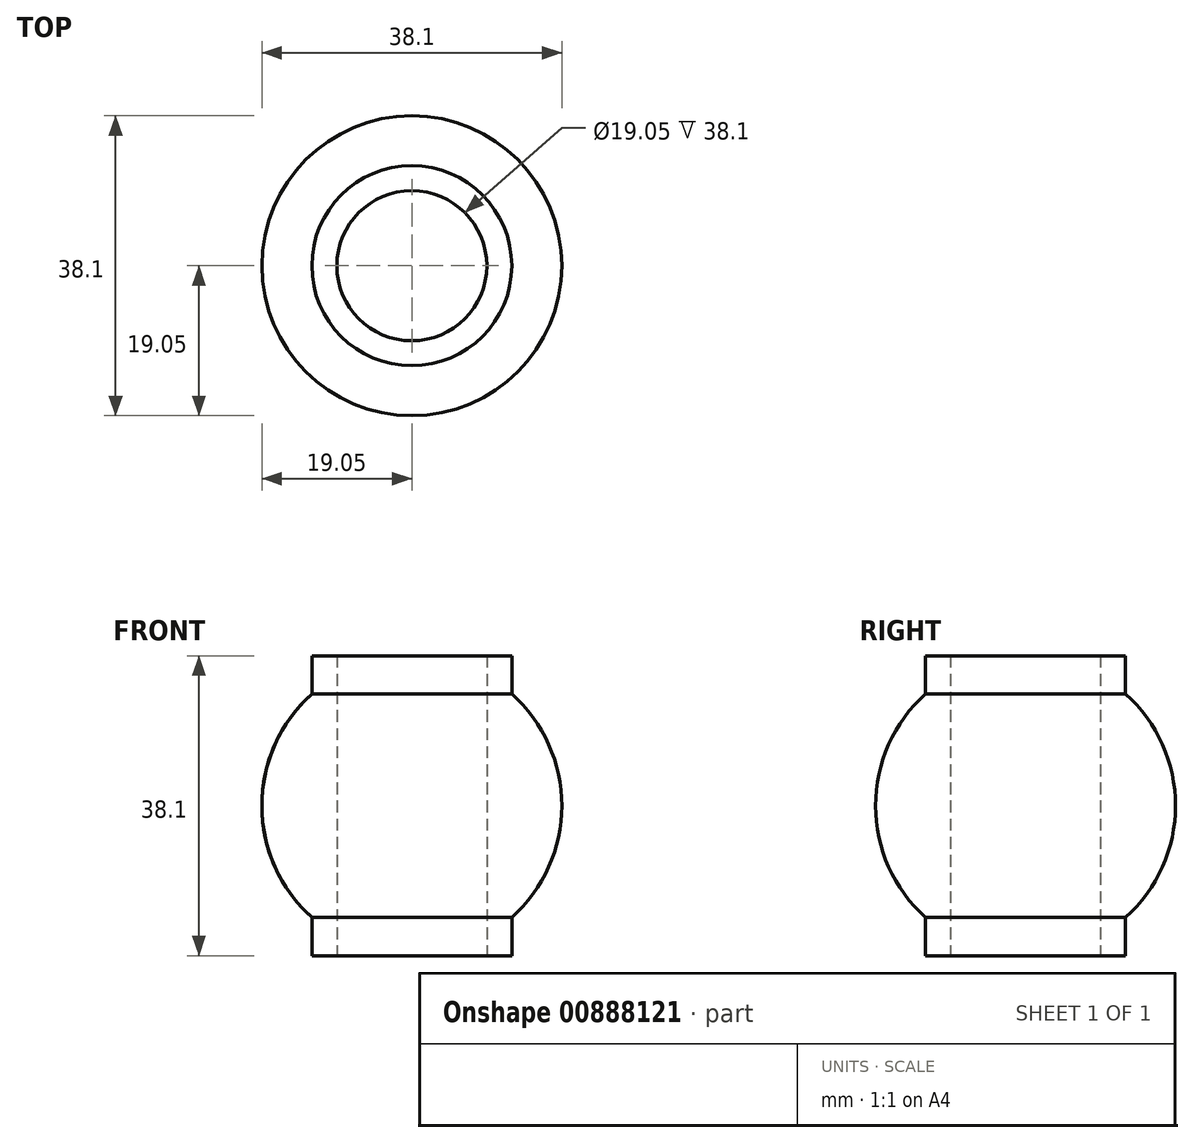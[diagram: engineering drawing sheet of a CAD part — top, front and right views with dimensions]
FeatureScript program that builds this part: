
annotation { "Feature Type Name" : "Feature", "Feature Type Description" : "" }
export const myFeature = defineFeature(function(context is Context, id is Id, definition is map)
    precondition{}
    {
        {
            var Q0;
            Q0=qCreatedBy(makeId("Front.planeOp"),FACE);
            var sketch = newSketch(context, id + "F0", { "sketchPlane" : qUnion([Q0])});
            skLineSegment(sketch, "E0", {"start": v(0, 0) * mm, "end": v(19.05, 0) * mm, "construction": true});
            skLineSegment(sketch, "E1", {"start": v(9.53, 0) * mm, "end": v(9.53, 19.05) * mm});
            skLineSegment(sketch, "E2", {"start": v(9.53, 19.05) * mm, "end": v(12.7, 19.05) * mm});
            skLineSegment(sketch, "E3", {"start": v(12.7, 19.05) * mm, "end": v(12.7, 14.2) * mm});
            skArc(sketch, "E4", {"start": v(12.7, 14.2) * mm, "mid": v(17.4, 7.78) * mm, "end": v(19.05, 0) * mm});
            skLineSegment(sketch, "E5.MirrorCS", {"start": v(9.53, 0) * mm, "end": v(9.53, -19.05) * mm});
            skLineSegment(sketch, "E6.MirrorCS", {"start": v(9.53, -19.05) * mm, "end": v(12.7, -19.05) * mm});
            skLineSegment(sketch, "E7.MirrorCS", {"start": v(12.7, -19.05) * mm, "end": v(12.7, -14.2) * mm});
            skArc(sketch, "E8.MirrorCS", {"start": v(12.7, -14.2) * mm, "mid": v(17.4, -7.78) * mm, "end": v(19.05, 0) * mm});
            skLineSegment(sketch, "E9", {"start": v(0, 0) * mm, "end": v(0, 19.05) * mm, "construction": true});
            skSolve(sketch);
        }
        {
            var Q0;
            Q0=makeQuery(id+"F0.imprint","IMPRINT",FACE,{"disambiguationData":[TD([[makeQuery(id+"F0.imprint","IMPRINT",EDGE,{"derivedFrom":sQuery(id+"F0.wireOp",EDGE,"E1")}),-1.0]])]});
            var Q1;
            Q1=sQuery(id+"F0.wireOp",EDGE,"E9");
            revolve(context, id + "F1", {"surfaceOperationType" : NewSurfaceOperationType.NEW, "entities" : qUnion([Q0]), "axis" : qUnion([Q1]), "revolveType" : RevolveType.FULL});
        }
    });
